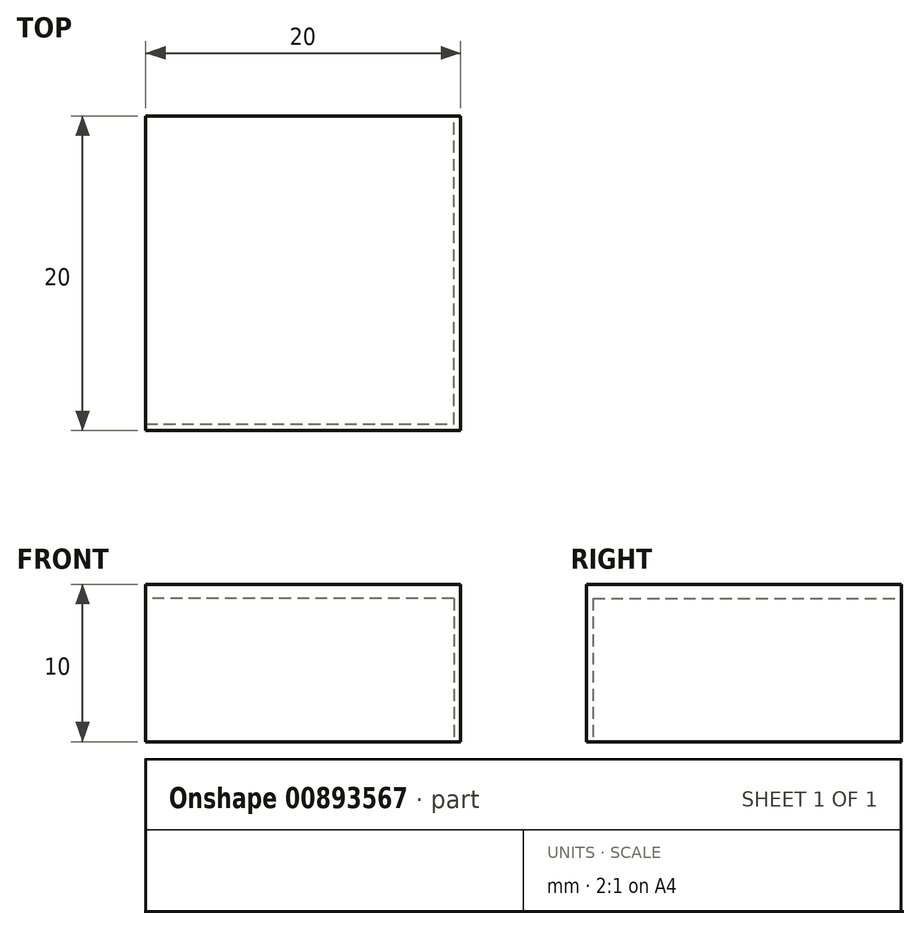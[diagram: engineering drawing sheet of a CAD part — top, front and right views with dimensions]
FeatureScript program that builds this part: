
annotation { "Feature Type Name" : "Feature", "Feature Type Description" : "" }
export const myFeature = defineFeature(function(context is Context, id is Id, definition is map)
    precondition{}
    {
        {
            assignVariable(context, id + "F0", {"name" : "height", "anyValue" : 10});
        }
        {
            assignVariable(context, id + "F1", {"name" : "layerHeight", "anyValue" : 0.3});
        }
        {
            assignVariable(context, id + "F2", {"name" : "roofWidth", "anyValue" : getVariable(context, 'layerHeight') * 3});
        }
        {
            var Q0;
            Q0=qCreatedBy(makeId("Top.planeOp"),FACE);
            var sketch = newSketch(context, id + "F3", { "sketchPlane" : qUnion([Q0])});
            skLineSegment(sketch, "E0.bottom", {"start": v(10, -10) * mm, "end": v(-10, -10) * mm});
            skLineSegment(sketch, "E0.top", {"start": v(10, 10) * mm, "end": v(-10, 10) * mm});
            skLineSegment(sketch, "E0.left", {"start": v(10, -10) * mm, "end": v(10, 10) * mm});
            skLineSegment(sketch, "E0.right", {"start": v(-10, -10) * mm, "end": v(-10, 10) * mm});
            skPoint(sketch, "E0.middle", {"position": v(0, 0) * mm});
            skSolve(sketch);
        }
        {
            var Q0;
            Q0=makeQuery(id+"F3.imprint","IMPRINT",FACE,{"disambiguationData":[TD([[makeQuery(id+"F3.imprint","IMPRINT",EDGE,{"derivedFrom":sQuery(id+"F3.wireOp",EDGE,"pCxOWCYt-oyMy-RZO5-76HX-edDlX2E49cpD.bottom")}),-1.0]])]});
            var Q1;
            Q1=makeQuery(id+"F3.imprint","IMPRINT",FACE,{"disambiguationData":[TD([[makeQuery(id+"F3.imprint","IMPRINT",EDGE,{"derivedFrom":sQuery(id+"F3.wireOp",EDGE,"E0.bottom")}),-1.0]])]});
            extrude(context, id + "F4", {"entities" : qUnion([Q0, Q1]), "depth" : (getVariable(context, 'height')) * mm, "offsetDistance" : 25 * mm});
        }
        {
            var Q0;
            Q0=makeQuery(id+"F4.opExtrude","CAP_FACE",FACE,{"disambiguationData":[OSD([sQuery(id+"F3.wireOp",EDGE,"E0.bottom"),sQuery(id+"F3.wireOp",EDGE,"E0.top"),sQuery(id+"F3.wireOp",EDGE,"E0.left"),sQuery(id+"F3.wireOp",EDGE,"E0.right")])],"isStart":true});
            var sketch = newSketch(context, id + "F5", { "sketchPlane" : qUnion([Q0])});
            skPoint(sketch, "E1.middle", {"position": v(-0.33, 0) * mm});
            skLineSegment(sketch, "E2", {"start": v(-10, 9.58) * mm, "end": v(9.58, 9.58) * mm});
            skLineSegment(sketch, "E3", {"start": v(9.58, 9.58) * mm, "end": v(9.58, -10) * mm});
            skSolve(sketch);
        }
        {
            var Q0;
            {var subQ0=sQuery(id+"F5.wireOp",EDGE,"E2");Q0=makeQuery(id+"F5.imprint","IMPRINT",FACE,{"disambiguationData":[TD([[makeQuery(id+"F5.imprint","IMPRINT",EDGE,{"derivedFrom":subQ0}),-1.0]])]});}
            extrude(context, id + "F6", {"entities" : qUnion([Q0]), "operationType" : NewBodyOperationType.REMOVE, "endBound" : BoundingType.UP_TO_NEXT, "oppositeDirection" : true, "depth" : 25 * mm, "hasOffset" : true, "offsetDistance" : (getVariable(context, 'roofWidth')) * mm});
        }
    });
